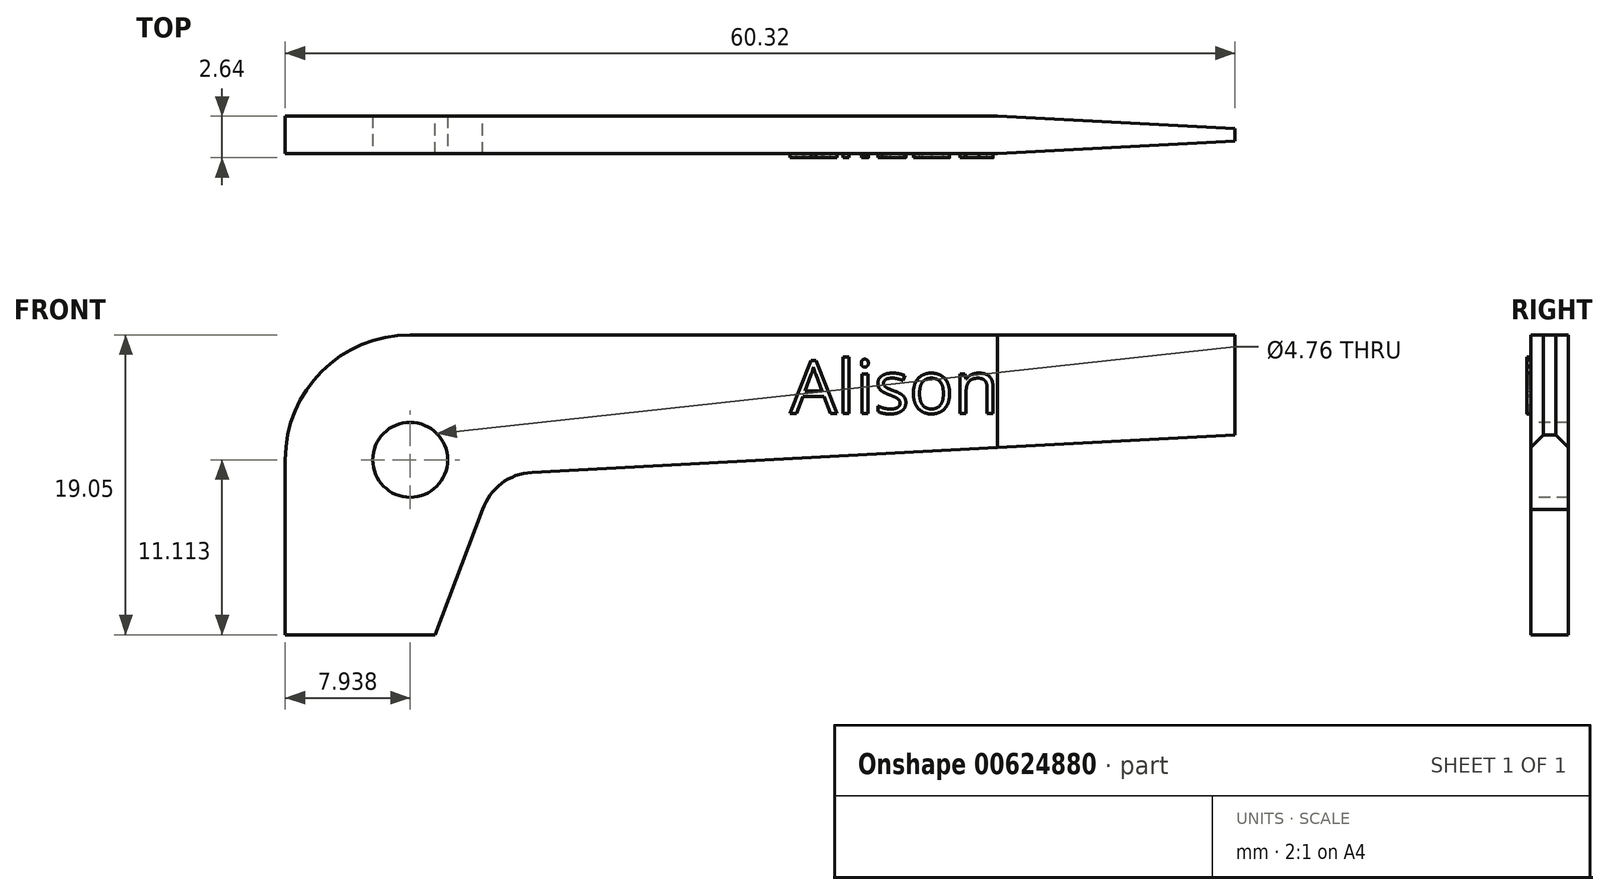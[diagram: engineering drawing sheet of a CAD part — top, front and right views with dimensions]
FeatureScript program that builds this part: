
annotation { "Feature Type Name" : "Feature", "Feature Type Description" : "" }
export const myFeature = defineFeature(function(context is Context, id is Id, definition is map)
    precondition{}
    {
        {
            var Q0;
            Q0=qCreatedBy(makeId("Front.planeOp"),FACE);
            var sketch = newSketch(context, id + "F0", { "sketchPlane" : qUnion([Q0])});
            skLineSegment(sketch, "E0.top", {"start": v(7.94, 19.05) * mm, "end": v(60.33, 19.05) * mm});
            skLineSegment(sketch, "E0.left", {"start": v(0, 0) * mm, "end": v(0, 11.11) * mm});
            skLineSegment(sketch, "E1", {"start": v(9.52, 0) * mm, "end": v(12.54, 7.94) * mm});
            skLineSegment(sketch, "E2", {"start": v(60.33, 12.7) * mm, "end": v(15.66, 10.31) * mm});
            skLineSegment(sketch, "E3", {"start": v(60.33, 19.05) * mm, "end": v(60.33, 12.7) * mm});
            skLineSegment(sketch, "E4", {"start": v(0, 0) * mm, "end": v(9.53, 0) * mm});
            skArc(sketch, "E5", {"start": v(15.66, 10.31) * mm, "mid": v(13.74, 9.6) * mm, "end": v(12.54, 7.94) * mm});
            skPoint(sketch, "E6.visualSharp", {"position": v(0, 19.05) * mm});
            skArc(sketch, "E6.filletArc", {"start": v(7.94, 19.05) * mm, "mid": v(2.32, 16.73) * mm, "end": v(0, 11.11) * mm});
            skSolve(sketch);
        }
        {
            var Q0;
            Q0 = qSketchRegion(id + "F0", true);
            extrude(context, id + "F1", {"entities" : qUnion([Q0]), "depth" : 2.38 * mm, "offsetDistance" : 25.4 * mm});
        }
        {
            var Q0;
            Q0=makeQuery(id+"F1.opExtrude","CAP_FACE",FACE,{"disambiguationData":[OSD([sQuery(id+"F0.wireOp",EDGE,"E0.top"),sQuery(id+"F0.wireOp",EDGE,"E0.left"),sQuery(id+"F0.wireOp",EDGE,"E1"),sQuery(id+"F0.wireOp",EDGE,"E2"),sQuery(id+"F0.wireOp",EDGE,"E3"),sQuery(id+"F0.wireOp",EDGE,"E4"),sQuery(id+"F0.wireOp",EDGE,"E5"),sQuery(id+"F0.wireOp",EDGE,"E6.filletArc")])],"isStart":false});
            var sketch = newSketch(context, id + "F2", { "sketchPlane" : qUnion([Q0])});
            skCircle(sketch, "E7", {"center": v(7.94, 11.11) * mm, "radius": 2.38 * mm});
            skSolve(sketch);
        }
        {
            var Q0;
            Q0=makeQuery(id+"F2.imprint","IMPRINT",FACE,{"disambiguationData":[TD([[makeQuery(id+"F2.imprint","IMPRINT",EDGE,{"derivedFrom":sQuery(id+"F2.wireOp",EDGE,"E7")}),1.0]])]});
            extrude(context, id + "F3", {"entities" : qUnion([Q0]), "operationType" : NewBodyOperationType.REMOVE, "oppositeDirection" : true, "depth" : 25.4 * mm, "offsetDistance" : 25.4 * mm});
        }
        {
            var Q0;
            Q0=makeQuery(id+"F1.opExtrude","SWEPT_FACE",FACE,{"disambiguationData":[OSD([sQuery(id+"F0.wireOp",EDGE,"E0.top")])]});
            var sketch = newSketch(context, id + "F4", { "sketchPlane" : qUnion([Q0])});
            skLineSegment(sketch, "E8", {"start": v(45.24, 0) * mm, "end": v(60.33, -0.8) * mm});
            skLineSegment(sketch, "E9", {"start": v(60.33, -0.8) * mm, "end": v(60.33, 0) * mm});
            skLineSegment(sketch, "E10", {"start": v(60.33, 0) * mm, "end": v(45.24, 0) * mm});
            skLineSegment(sketch, "E11.MirrorCS", {"start": v(45.24, -2.38) * mm, "end": v(60.33, -1.59) * mm});
            skLineSegment(sketch, "E12.MirrorCS", {"start": v(60.33, -2.38) * mm, "end": v(45.24, -2.38) * mm});
            skLineSegment(sketch, "E13.MirrorCS", {"start": v(60.33, -1.59) * mm, "end": v(60.33, -2.38) * mm});
            skSolve(sketch);
        }
        {
            var Q0;
            Q0=makeQuery(id+"F4.imprint","IMPRINT",FACE,{"disambiguationData":[TD([[makeQuery(id+"F4.imprint","IMPRINT",EDGE,{"derivedFrom":sQuery(id+"F4.wireOp",EDGE,"E8")}),1.0]])]});
            var Q1;
            Q1=makeQuery(id+"F4.imprint","IMPRINT",FACE,{"disambiguationData":[TD([[makeQuery(id+"F4.imprint","IMPRINT",EDGE,{"derivedFrom":sQuery(id+"F4.wireOp",EDGE,"E11.MirrorCS")}),-1.0]])]});
            extrude(context, id + "F5", {"entities" : qUnion([Q0, Q1]), "operationType" : NewBodyOperationType.REMOVE, "oppositeDirection" : true, "depth" : 25.4 * mm, "offsetDistance" : 25.4 * mm});
        }
        {
            var Q0;
            Q0=makeQuery(id+"F1.opExtrude","CAP_FACE",FACE,{"disambiguationData":[OSD([sQuery(id+"F0.wireOp",EDGE,"E0.top"),sQuery(id+"F0.wireOp",EDGE,"E0.left"),sQuery(id+"F0.wireOp",EDGE,"E1"),sQuery(id+"F0.wireOp",EDGE,"E2"),sQuery(id+"F0.wireOp",EDGE,"E3"),sQuery(id+"F0.wireOp",EDGE,"E4"),sQuery(id+"F0.wireOp",EDGE,"E5"),sQuery(id+"F0.wireOp",EDGE,"E6.filletArc")])],"isStart":false});
            var sketch = newSketch(context, id + "F6", { "sketchPlane" : qUnion([Q0])});
            skText(sketch, "E14", { "text": "Alison ", "fontName": "OpenSans-Regular.ttf"});
            const initialGuessF6  = {"E14": [0.03207, 0.01407, 1, 0, 0.00337]};
            skSetInitialGuess(sketch, initialGuessF6);
            skSolve(sketch);
        }
        {
            var Q0;
            Q0 = qSketchRegion(id + "F6", true);
            extrude(context, id + "F7", {"entities" : qUnion([Q0]), "operationType" : NewBodyOperationType.ADD, "depth" : 0.25 * mm, "offsetDistance" : 25.4 * mm});
        }
    });
